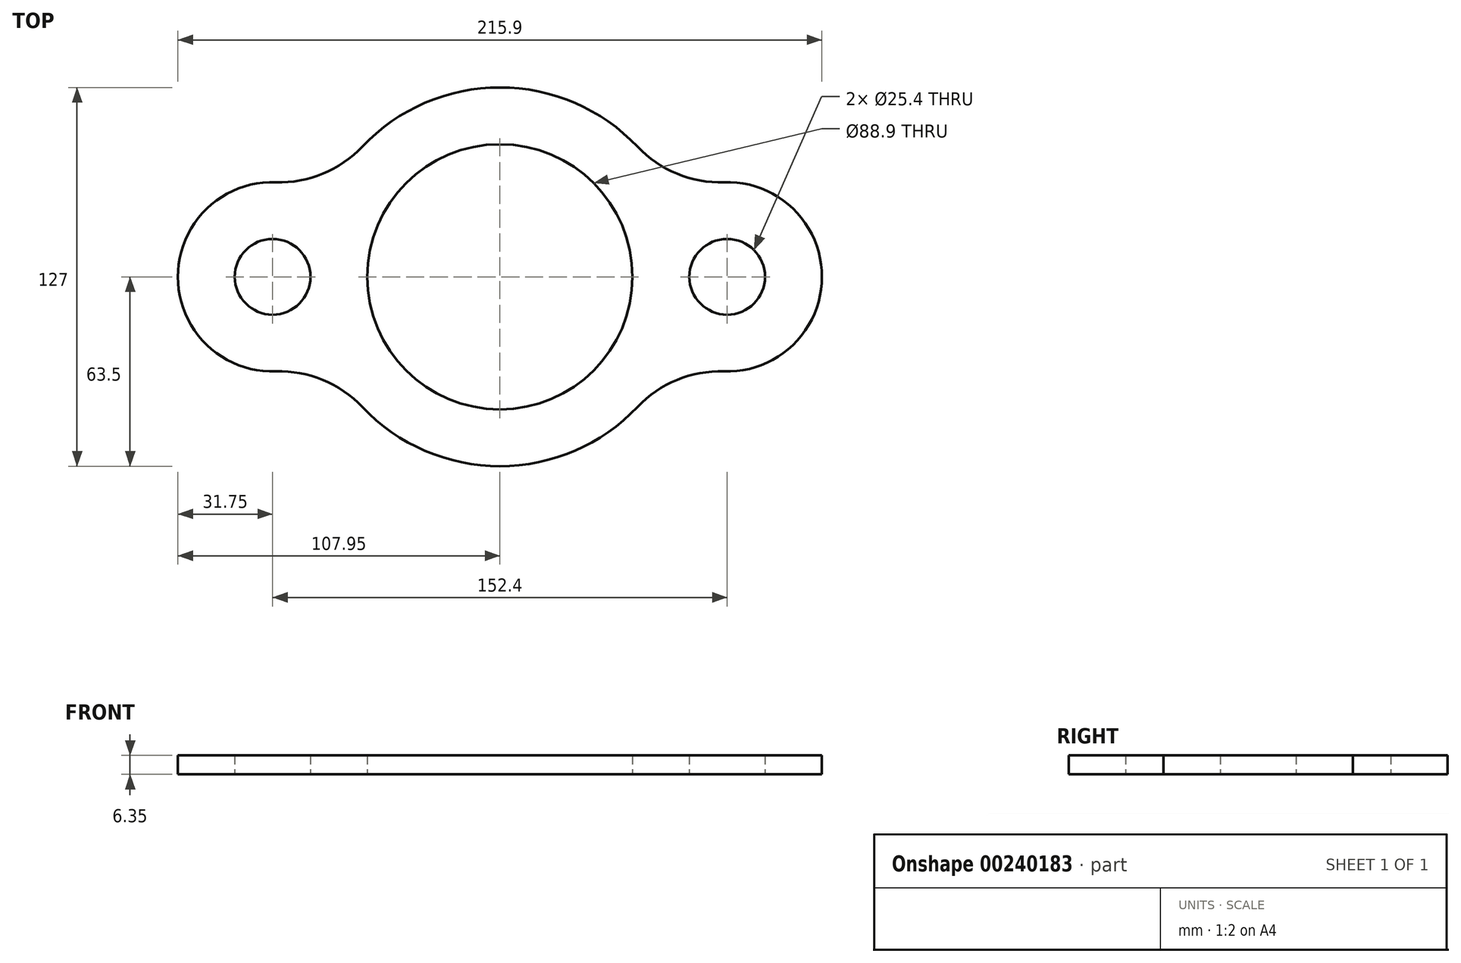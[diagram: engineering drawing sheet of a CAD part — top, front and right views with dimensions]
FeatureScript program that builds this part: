
annotation { "Feature Type Name" : "Feature", "Feature Type Description" : "" }
export const myFeature = defineFeature(function(context is Context, id is Id, definition is map)
    precondition{}
    {
        {
            var Q0;
            Q0=qCreatedBy(makeId("Top.planeOp"),FACE);
            var sketch = newSketch(context, id + "F0", { "sketchPlane" : qUnion([Q0])});
            skCircle(sketch, "E0", {"center": v(-76.2, 0) * mm, "radius": 12.7 * mm});
            skCircle(sketch, "E1", {"center": v(0, 0) * mm, "radius": 44.45 * mm});
            skCircle(sketch, "E2", {"center": v(76.2, 0) * mm, "radius": 12.7 * mm});
            skArc(sketch, "E3", {"start": v(-46.14, -43.63) * mm, "mid": v(0, -63.5) * mm, "end": v(46.14, -43.63) * mm});
            skArc(sketch, "E4", {"start": v(-75.12, 31.73) * mm, "mid": v(-107.95, 0) * mm, "end": v(-75.12, -31.73) * mm});
            skArc(sketch, "E5", {"start": v(75.12, -31.73) * mm, "mid": v(107.95, 0) * mm, "end": v(75.12, 31.73) * mm});
            skArc(sketch, "E6.trimOffspring", {"start": v(46.14, 43.63) * mm, "mid": v(0, 63.5) * mm, "end": v(-46.14, 43.63) * mm});
            skArc(sketch, "E7", {"start": v(-46.14, -43.63) * mm, "mid": v(-59.35, -34.56) * mm, "end": v(-75.12, -31.73) * mm});
            skArc(sketch, "E8", {"start": v(-75.12, 31.73) * mm, "mid": v(-59.35, 34.56) * mm, "end": v(-46.14, 43.63) * mm});
            skArc(sketch, "E9", {"start": v(46.14, 43.63) * mm, "mid": v(59.35, 34.56) * mm, "end": v(75.12, 31.73) * mm});
            skArc(sketch, "E10", {"start": v(75.12, -31.73) * mm, "mid": v(59.35, -34.56) * mm, "end": v(46.14, -43.63) * mm});
            skSolve(sketch);
        }
        {
            var Q0;
            Q0 = qSketchRegion(id + "F0", true);
            extrude(context, id + "F1", {"entities" : qUnion([Q0]), "depth" : 6.35 * mm});
        }
    });
